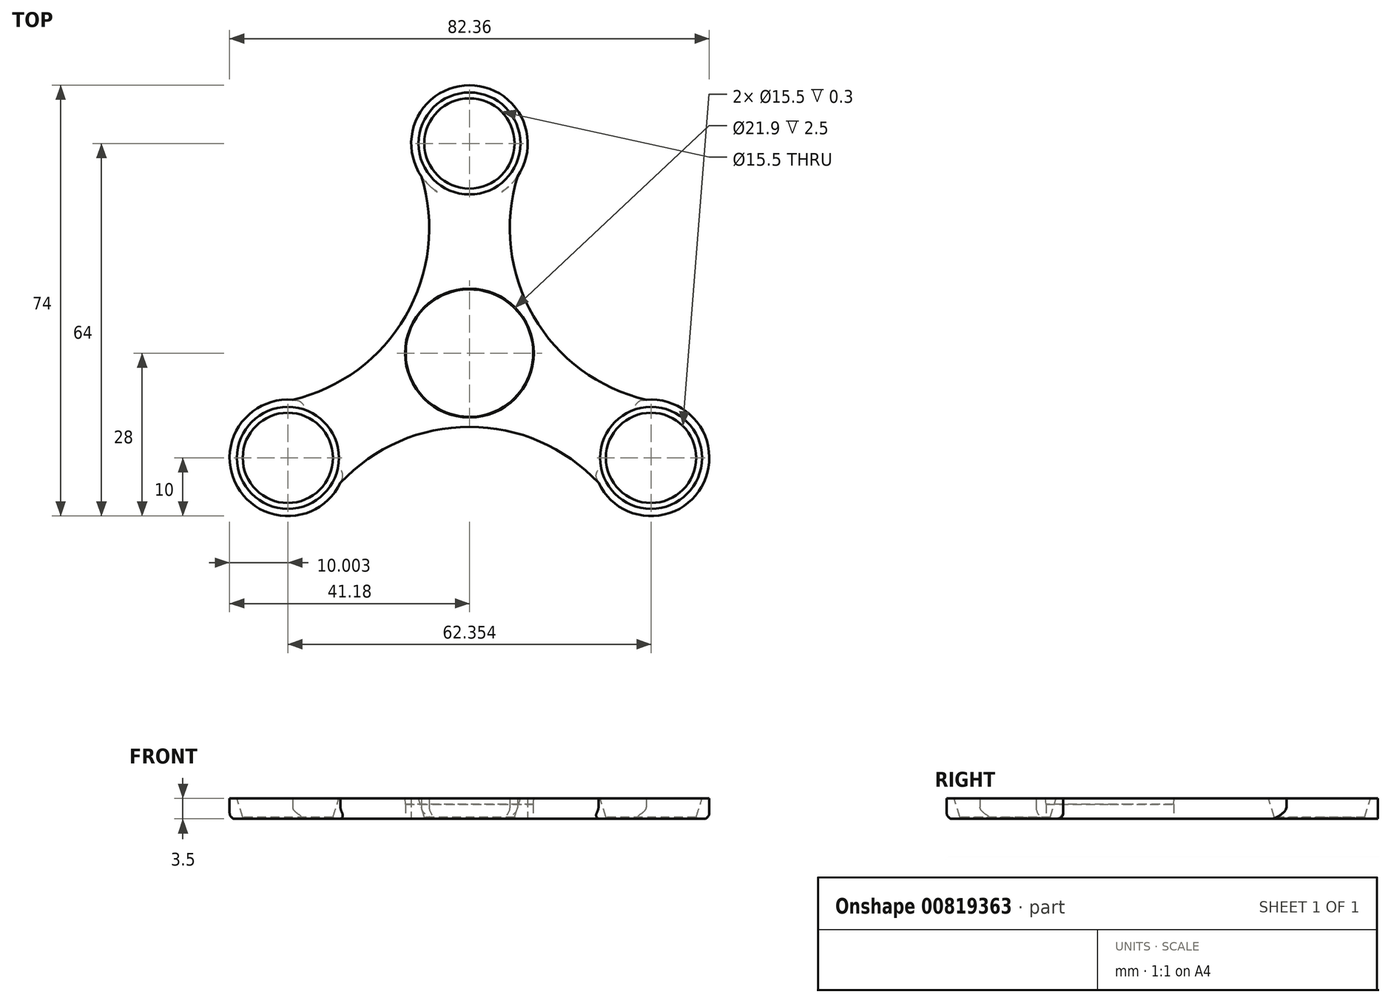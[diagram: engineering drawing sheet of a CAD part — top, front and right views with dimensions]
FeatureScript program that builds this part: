
annotation { "Feature Type Name" : "Feature", "Feature Type Description" : "" }
export const myFeature = defineFeature(function(context is Context, id is Id, definition is map)
    precondition{}
    {
        {
            var Q0;
            Q0=qCreatedBy(makeId("Top.planeOp"),FACE);
            var sketch = newSketch(context, id + "F0", { "sketchPlane" : qUnion([Q0])});
            skCircle(sketch, "E0", {"center": v(0, 0) * mm, "radius": 10.95 * mm});
            skCircle(sketch, "E1", {"center": v(0, 36) * mm, "radius": 7.75 * mm});
            skArc(sketch, "E2", {"start": v(8.23, 30.32) * mm, "mid": v(0, 46) * mm, "end": v(-8.23, 30.32) * mm});
            skCircle(sketch, "E3.1.0", {"center": v(-31.18, -18) * mm, "radius": 7.75 * mm});
            skArc(sketch, "E3.1.1", {"start": v(-30.37, -8.03) * mm, "mid": v(-40.76, -20.87) * mm, "end": v(-25.02, -25.88) * mm});
            skCircle(sketch, "E3.2.0", {"center": v(31.18, -18) * mm, "radius": 7.75 * mm});
            skArc(sketch, "E3.2.1", {"start": v(22.14, -22.29) * mm, "mid": v(39.84, -23) * mm, "end": v(30.37, -8.03) * mm});
            skArc(sketch, "E4", {"start": v(-30.37, -8.03) * mm, "mid": v(-10.97, 6.34) * mm, "end": v(-8.23, 30.32) * mm});
            skArc(sketch, "E5.1.0", {"start": v(22.14, -22.29) * mm, "mid": v(0, -12.67) * mm, "end": v(-22.14, -22.29) * mm});
            skArc(sketch, "E5.2.0", {"start": v(8.23, 30.32) * mm, "mid": v(10.97, 6.34) * mm, "end": v(30.37, -8.03) * mm});
            skPoint(sketch, "E6.orphan", {"position": v(-34.93, -8.73) * mm});
            skPoint(sketch, "E7.orphan", {"position": v(25.02, -25.88) * mm});
            skPoint(sketch, "E8.orphan", {"position": v(34.93, -8.73) * mm});
            skPoint(sketch, "E9.orphan", {"position": v(9.9, 34.61) * mm});
            skPoint(sketch, "E10.orphan", {"position": v(-9.9, 34.61) * mm});
            skArc(sketch, "E11.2.0", {"start": v(-30.37, -8.03) * mm, "mid": v(-39.84, -23) * mm, "end": v(-22.14, -22.29) * mm});
            skSolve(sketch);
        }
        {
            var Q0;
            Q0 = qSketchRegion(id + "F0", true);
            extrude(context, id + "F1", {"entities" : qUnion([Q0]), "depth" : 3.5 * mm, "offsetDistance" : 25 * mm});
        }
        {
            var Q0;
            Q0=makeQuery(id+"F1.opExtrude","CAP_EDGE",EDGE,{"disambiguationData":[OSD([sQuery(id+"F0.wireOp",EDGE,"E3.1.0")])],"isStart":false});
            var Q1;
            Q1=makeQuery(id+"F1.opExtrude","CAP_EDGE",EDGE,{"disambiguationData":[OSD([sQuery(id+"F0.wireOp",EDGE,"E3.2.0")])],"isStart":false});
            var Q2;
            Q2=makeQuery(id+"F1.opExtrude","CAP_EDGE",EDGE,{"disambiguationData":[OSD([sQuery(id+"F0.wireOp",EDGE,"E1")])],"isStart":false});
            chamfer(context, id + "F2", {"entities" : qUnion([Q0, Q1, Q2]), "chamferType" : ChamferType.TWO_OFFSETS, "width1" : 3.2 * mm, "oppositeDirection" : false, "width2" : 1 * mm, "tangentPropagation" : true});
        }
        {
            var Q0;
            Q0=makeQuery(id+"F1.opExtrude","CAP_EDGE",EDGE,{"disambiguationData":[OSD([sQuery(id+"F0.wireOp",EDGE,"E4")])],"isStart":true});
            var Q1;
            Q1=makeQuery(id+"F1.opExtrude","CAP_EDGE",EDGE,{"disambiguationData":[OSD([sQuery(id+"F0.wireOp",EDGE,"E5.1.0")])],"isStart":true});
            var Q2;
            Q2=makeQuery(id+"F1.opExtrude","CAP_EDGE",EDGE,{"disambiguationData":[OSD([sQuery(id+"F0.wireOp",EDGE,"E5.2.0")])],"isStart":true});
            fillet(context, id + "F3", {"entities" : qUnion([Q0, Q1, Q2]), "radius" : 2 * mm, "tangentPropagation" : true, "allowEdgeOverflow" : false});
        }
        {
            var Q0;
            Q0=makeQuery(id+"F1.opExtrude","CAP_EDGE",EDGE,{"disambiguationData":[OSD([sQuery(id+"F0.wireOp",EDGE,"E0")])],"isStart":false});
            chamfer(context, id + "F4", {"entities" : qUnion([Q0]), "chamferType" : ChamferType.TWO_OFFSETS, "width1" : 1 * mm, "oppositeDirection" : false, "width2" : .1 * mm, "tangentPropagation" : true});
        }
        {
            var Q0;
            Q0=makeQuery(id+"F1.opExtrude","CAP_EDGE",EDGE,{"disambiguationData":[OSD([sQuery(id+"F0.wireOp",EDGE,"E11.2.0")])],"isStart":true});
            var Q1;
            Q1=makeQuery(id+"F1.opExtrude","CAP_EDGE",EDGE,{"disambiguationData":[OSD([sQuery(id+"F0.wireOp",EDGE,"E3.2.1")])],"isStart":true});
            var Q2;
            Q2=makeQuery(id+"F1.opExtrude","CAP_EDGE",EDGE,{"disambiguationData":[OSD([sQuery(id+"F0.wireOp",EDGE,"E2")])],"isStart":true});
            fillet(context, id + "F5", {"entities" : qUnion([Q0, Q1, Q2]), "radius" : 1 * mm, "tangentPropagation" : true, "allowEdgeOverflow" : false});
        }
    });
